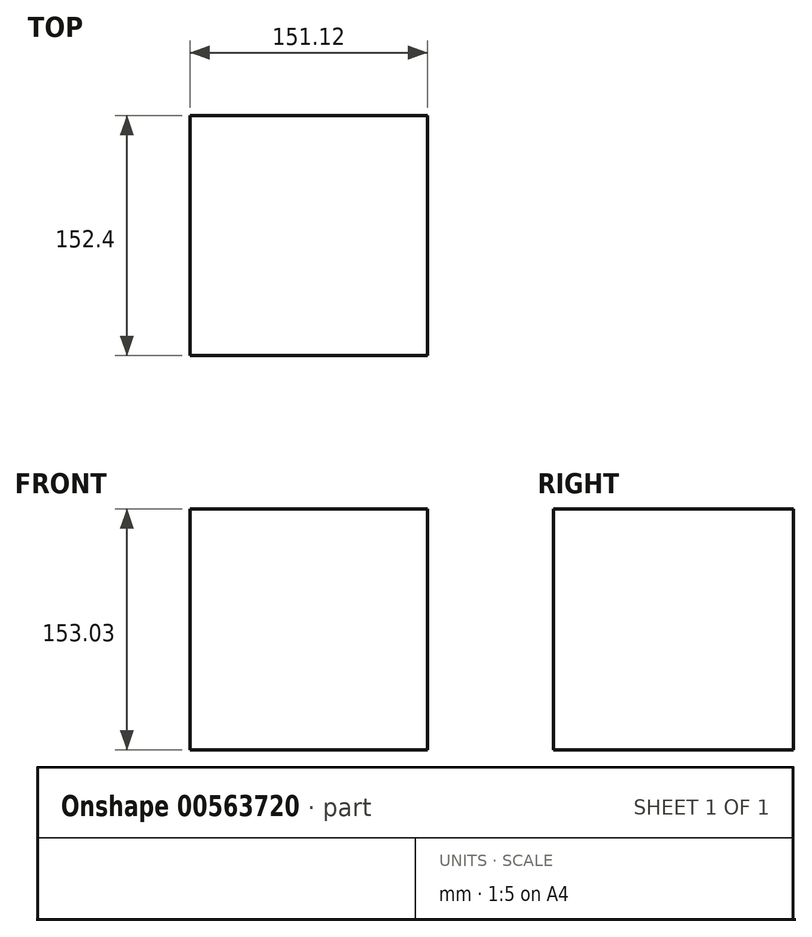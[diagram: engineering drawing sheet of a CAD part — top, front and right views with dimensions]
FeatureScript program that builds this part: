
annotation { "Feature Type Name" : "Feature", "Feature Type Description" : "" }
export const myFeature = defineFeature(function(context is Context, id is Id, definition is map)
    precondition{}
    {
        {
            var Q0;
            Q0=qCreatedBy(makeId("Front.planeOp"),FACE);
            var sketch = newSketch(context, id + "F0", { "sketchPlane" : qUnion([Q0])});
            skLineSegment(sketch, "E0.bottom", {"start": v(-76.06, 76.12) * mm, "end": v(75.06, 76.12) * mm});
            skLineSegment(sketch, "E0.top", {"start": v(-76.06, -76.9) * mm, "end": v(75.06, -76.9) * mm});
            skLineSegment(sketch, "E0.left", {"start": v(-76.06, 76.12) * mm, "end": v(-76.06, -76.9) * mm});
            skLineSegment(sketch, "E0.right", {"start": v(75.06, 76.12) * mm, "end": v(75.06, -76.9) * mm});
            skSolve(sketch);
        }
        {
            var Q0;
            Q0=makeQuery(id+"F0.imprint","IMPRINT",FACE,{"disambiguationData":[TD([[makeQuery(id+"F0.imprint","IMPRINT",EDGE,{"derivedFrom":sQuery(id+"F0.wireOp",EDGE,"E0.bottom")}),-1.0]])]});
            extrude(context, id + "F1", {"entities" : qUnion([Q0]), "depth" : 152.4 * mm, "offsetDistance" : 25.4 * mm});
        }
    });
